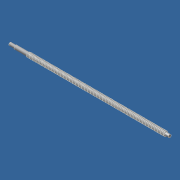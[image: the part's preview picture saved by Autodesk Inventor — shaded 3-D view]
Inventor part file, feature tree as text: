
AUTODESK INVENTOR PART (.ipt)
format: ipt  version: 2013 SP2 (Build 170200200, 200)  size: 733,696 bytes
history: native  units: in
note: dims shown in document units (in); Inventor stores cm internally (conversion verified against a paired STEP export)
features: sketch x2, revolve x1, helix x1, projected_geometry x1
ambient origin geometry x8: Origin, YZ Plane, XZ Plane, XY Plane, X Axis, Y Axis, Z Axis, Center Point
bodies: Solid1 (feature_tree)
feature tree (5):
  revolve  "Revolution1"  [1 undecoded]
  helix  "Coil1"  [1 undecoded]
  sketch  "Sketch1"  dims[d0=16.8541in d1=0.315in d2=0.3937in]
  sketch  "Sketch2"  dims[d3=1.9309in d4=0.3937in d5=0.4724in d6=0.315in d7=0.5906in d8=90.0deg d9=0.1181in d12=0.5315in d13=0.2362in d14=0.1575in d15=16.9291in d16=0.3937in d17=0.0in d18=90.0deg d19=90.0deg d20=0.0in d21=0.0in]
  projected_geometry  "Project Cut Edges1"
note: 2 required parameter values undecoded (feature->parameter linkage not recoverable at this tier; creation-order binding heuristic only, values carry confidence <= 0.55)